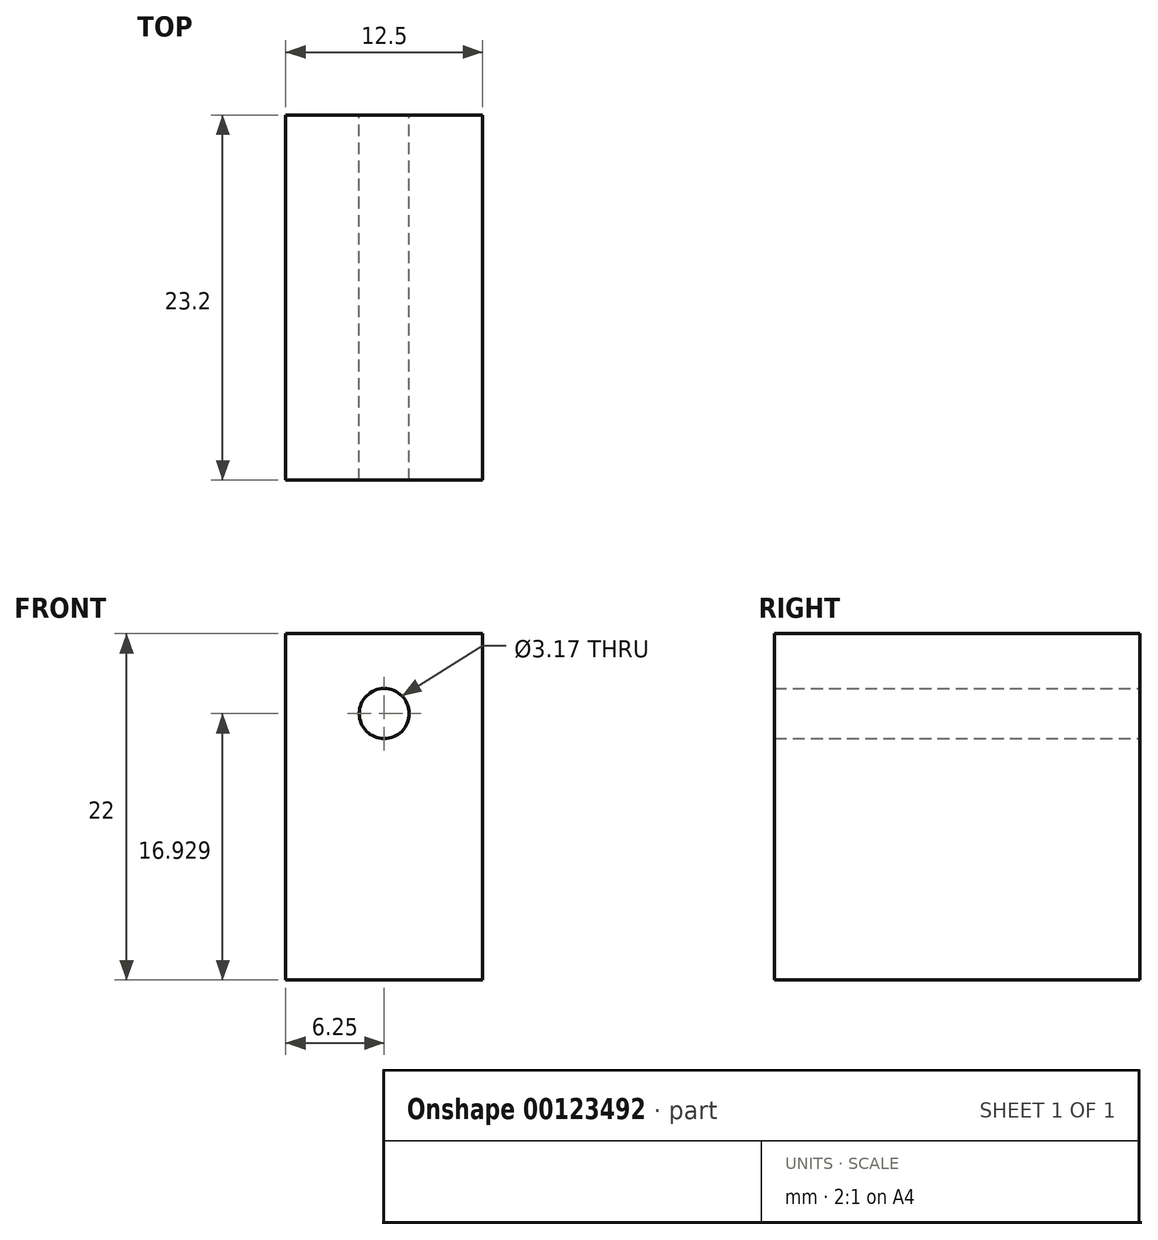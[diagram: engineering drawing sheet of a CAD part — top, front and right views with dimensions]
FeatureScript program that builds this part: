
annotation { "Feature Type Name" : "Feature", "Feature Type Description" : "" }
export const myFeature = defineFeature(function(context is Context, id is Id, definition is map)
    precondition{}
    {
        {
            var Q0;
            Q0=qCreatedBy(makeId("Top.planeOp"),FACE);
            var sketch = newSketch(context, id + "F0", { "sketchPlane" : qUnion([Q0])});
            skLineSegment(sketch, "E0.left", {"start": v(0, 0) * mm, "end": v(0, 0) * mm});
            skLineSegment(sketch, "E0.right", {"start": v(4.53, 0) * mm, "end": v(4.53, 0) * mm});
            skLineSegment(sketch, "E1.bottom", {"start": v(0, 0) * mm, "end": v(12.5, 0) * mm});
            skLineSegment(sketch, "E1.top", {"start": v(0, 23.2) * mm, "end": v(12.5, 23.2) * mm});
            skLineSegment(sketch, "E1.left", {"start": v(0, 0) * mm, "end": v(0, 23.2) * mm});
            skLineSegment(sketch, "E1.right", {"start": v(12.5, 0) * mm, "end": v(12.5, 23.2) * mm});
            skSolve(sketch);
        }
        {
            var Q0;
            Q0 = qSketchRegion(id + "F0", true);
            extrude(context, id + "F1", {"entities" : qUnion([Q0]), "depth" : 22 * mm});
        }
        {
            var Q0;
            Q0=makeQuery(id+"F1.opExtrude","SWEPT_FACE",FACE,{"disambiguationData":[OSD([sQuery(id+"F0.wireOp",EDGE,"E1.top")])]});
            var sketch = newSketch(context, id + "F2", { "sketchPlane" : qUnion([Q0])});
            skCircle(sketch, "E2", {"center": v(-6.25, 16.93) * mm, "radius": 1.59 * mm});
            skPoint(sketch, "E2.centerSnap0", {"position": v(-6.25, 22) * mm});
            skSolve(sketch);
        }
        {
            var Q0;
            Q0=makeQuery(id+"F2.imprint","IMPRINT",FACE,{"disambiguationData":[TD([[makeQuery(id+"F2.imprint","IMPRINT",EDGE,{"derivedFrom":sQuery(id+"F2.wireOp",EDGE,"E2")}),1.0]])]});
            extrude(context, id + "F3", {"entities" : qUnion([Q0]), "operationType" : NewBodyOperationType.REMOVE, "oppositeDirection" : true, "depth" : 25 * mm});
        }
    });
